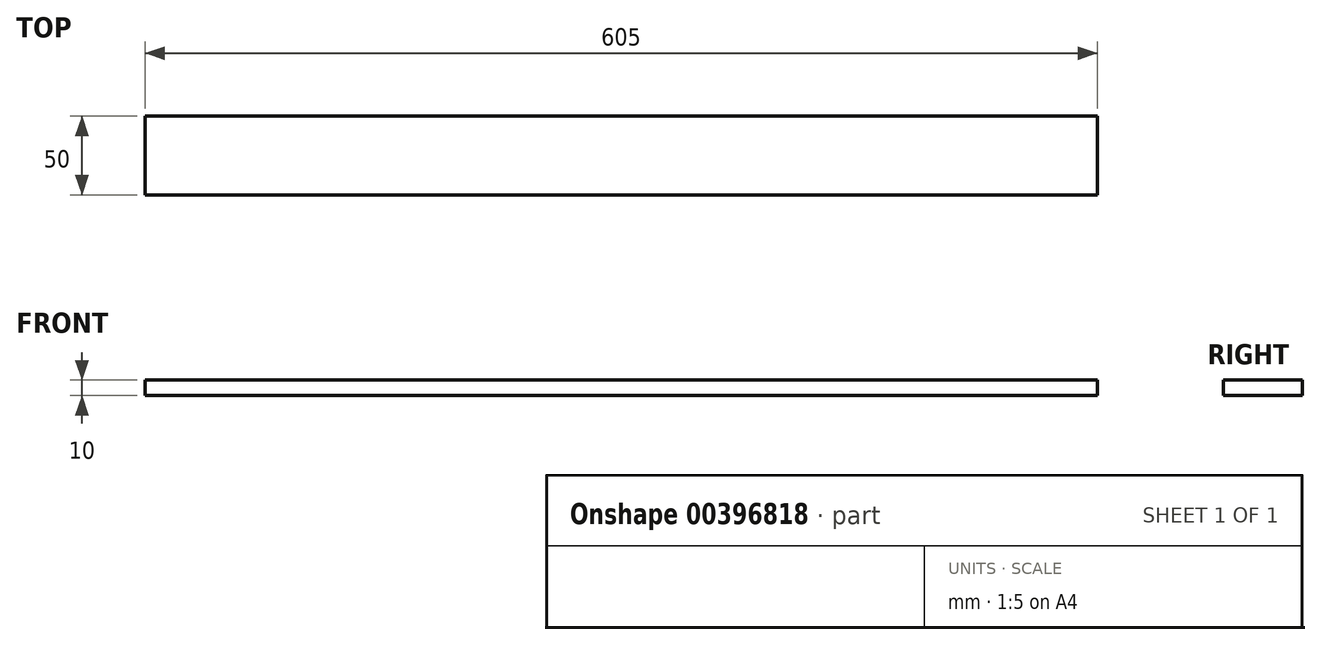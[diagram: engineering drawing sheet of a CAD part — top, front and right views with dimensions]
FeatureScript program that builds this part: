
annotation { "Feature Type Name" : "Feature", "Feature Type Description" : "" }
export const myFeature = defineFeature(function(context is Context, id is Id, definition is map)
    precondition{}
    {
        {
            var Q0;
            Q0=qCreatedBy(makeId("Right.planeOp"),FACE);
            var sketch = newSketch(context, id + "F0", { "sketchPlane" : qUnion([Q0])});
            skLineSegment(sketch, "E0.bottom", {"start": v(25, 5) * mm, "end": v(-25, 5) * mm});
            skLineSegment(sketch, "E0.top", {"start": v(25, -5) * mm, "end": v(-25, -5) * mm});
            skLineSegment(sketch, "E0.left", {"start": v(25, 5) * mm, "end": v(25, -5) * mm});
            skLineSegment(sketch, "E0.right", {"start": v(-25, 5) * mm, "end": v(-25, -5) * mm});
            skPoint(sketch, "E0.middle", {"position": v(0, 0) * mm});
            skSolve(sketch);
        }
        {
            var Q0;
            Q0=qSketchRegion(id+"F0",true);
            extrude(context, id + "F1", {"entities" : qUnion([Q0]), "endBound" : BoundingType.SYMMETRIC, "depth" : 605 * mm});
        }
    });
